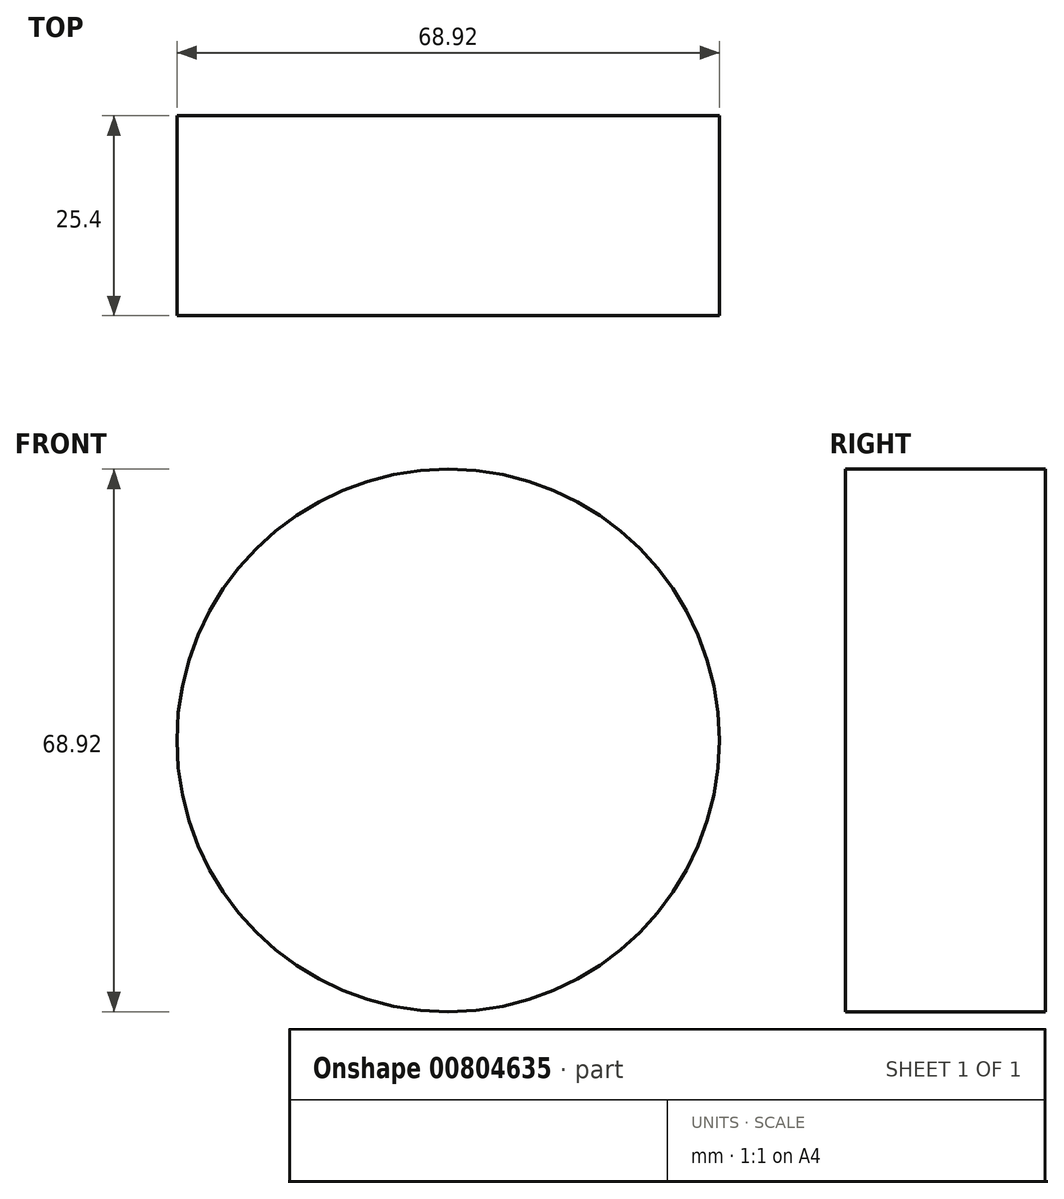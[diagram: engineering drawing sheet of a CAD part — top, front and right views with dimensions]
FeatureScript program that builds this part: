
annotation { "Feature Type Name" : "Feature", "Feature Type Description" : "" }
export const myFeature = defineFeature(function(context is Context, id is Id, definition is map)
    precondition{}
    {
        {
            var Q0;
            Q0=qCreatedBy(makeId("Front.planeOp"),FACE);
            var sketch = newSketch(context, id + "F0", { "sketchPlane" : qUnion([Q0])});
            skCircle(sketch, "E0", {"center": v(0, 0) * mm, "radius": 34.46 * mm});
            skSolve(sketch);
        }
        {
            var Q0;
            Q0=makeQuery(id+"F0.imprint","IMPRINT",FACE,{"disambiguationData":[TD([[makeQuery(id+"F0.imprint","IMPRINT",EDGE,{"derivedFrom":sQuery(id+"F0.wireOp",EDGE,"E0")}),1.0]])]});
            extrude(context, id + "F1", {"entities" : qUnion([Q0]), "depth" : 25.4 * mm, "offsetDistance" : 25.4 * mm});
        }
    });
